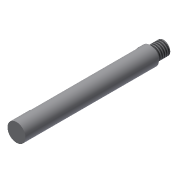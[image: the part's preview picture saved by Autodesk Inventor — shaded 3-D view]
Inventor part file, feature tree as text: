
AUTODESK INVENTOR PART (.ipt)
format: ipt  version: 2015 (Build 190159000, 159)  size: 103,424 bytes
history: native  units: mm
features: extrude x6, sketch x6, thread x1
ambient origin geometry x8: Origin, YZ Plane, XZ Plane, XY Plane, X Axis, Y Axis, Z Axis, Center Point
bodies: Solid1 (feature_tree)
feature tree (13):
  extrude  "Extrusion1"  Depth=65.0mm TaperAngle=0.0deg
  extrude  "Extrusion2"  Depth=8.5mm TaperAngle=0.0deg
  extrude  "Extrusion3"  Depth=8.5mm TaperAngle=0.0deg
  extrude  "Extrusion4"  Depth=8.5mm TaperAngle=0.0deg
  extrude  "Extrusion5"  Depth=6.0mm
  extrude  "Extrusion6"  Depth=10.0mm TaperAngle=0.0deg
  thread  "Thread1"  [1 undecoded]
  sketch  "Sketch1"  dims[d1=6.0mm d2=65.0mm d3=0.0mm]
  sketch  "Sketch2"  dims[d5=8.5mm d6=0.0mm d7=8.5mm d8=0.0mm]
  sketch  "Sketch3"  dims[d9=8.0mm d10=8.5mm d11=0.0mm]
  sketch  "Sketch4"  dims[d12=8.0mm d13=8.5mm d14=0.0mm]
  sketch  "Sketch5"  dims[d15=6.0mm d16=8.0mm]
  sketch  "Sketch6"  dims[d17=6.0mm d18=0.0mm d19=10.0mm d20=0.0mm]
note: 1 required parameter value undecoded (feature->parameter linkage not recoverable at this tier; creation-order binding heuristic only, values carry confidence <= 0.55)
